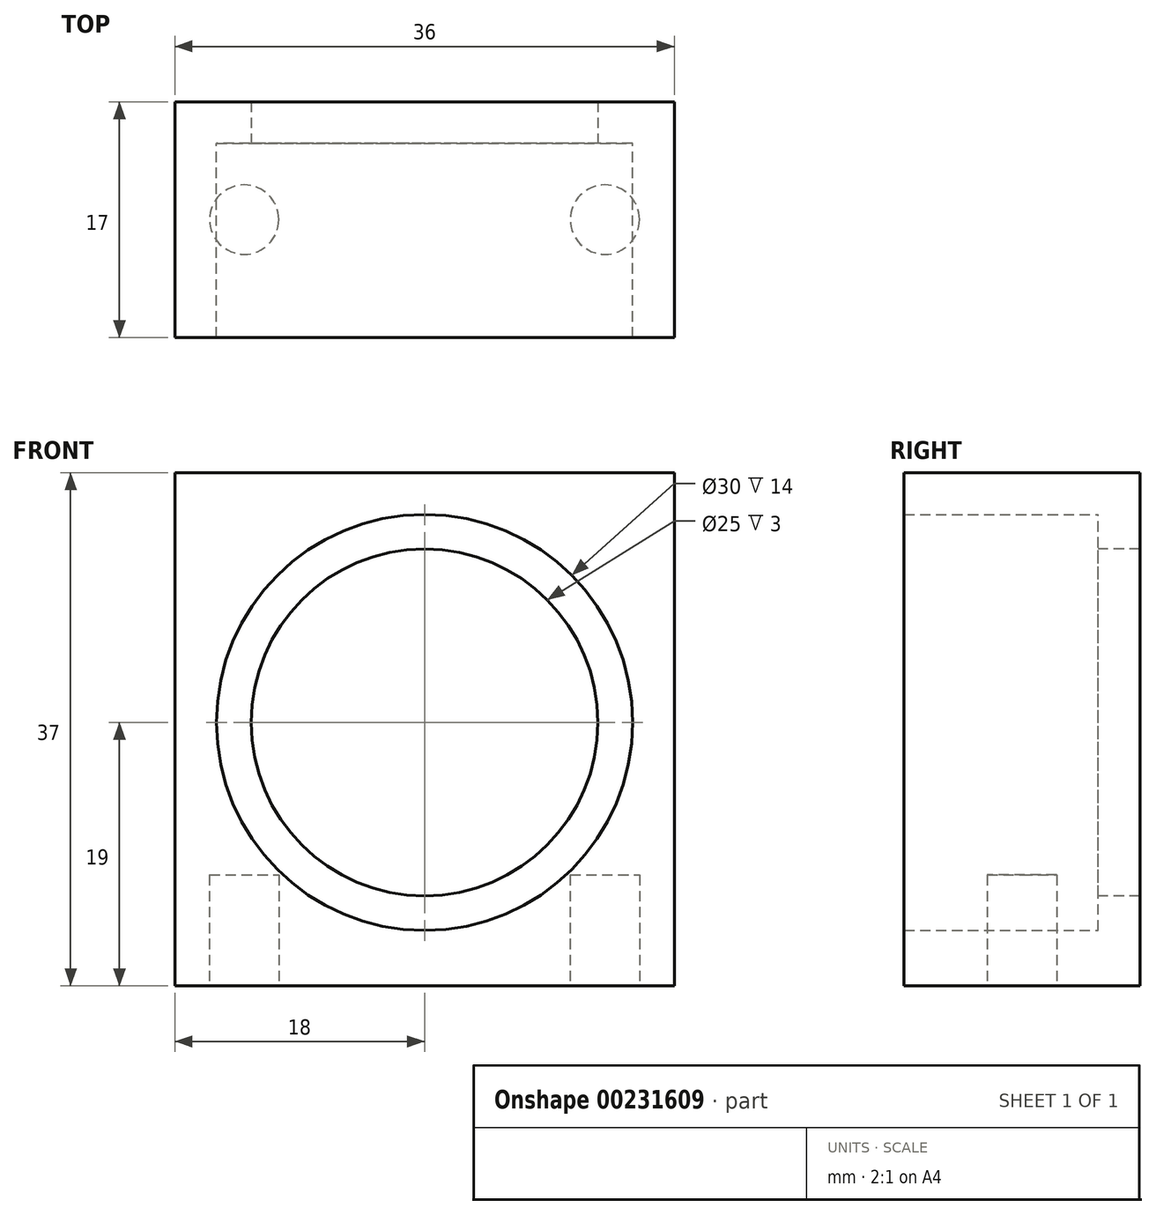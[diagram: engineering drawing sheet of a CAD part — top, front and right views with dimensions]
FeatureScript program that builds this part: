
annotation { "Feature Type Name" : "Feature", "Feature Type Description" : "" }
export const myFeature = defineFeature(function(context is Context, id is Id, definition is map)
    precondition{}
    {
        {
            var Q0;
            Q0=qCreatedBy(makeId("Front.planeOp"),FACE);
            var sketch = newSketch(context, id + "F0", { "sketchPlane" : qUnion([Q0])});
            skCircle(sketch, "E0", {"center": v(0, 0) * mm, "radius": 12.5 * mm});
            skCircle(sketch, "E1", {"center": v(0, 0) * mm, "radius": 15 * mm});
            skLineSegment(sketch, "E2.bottom", {"start": v(-18, 18) * mm, "end": v(18, 18) * mm});
            skLineSegment(sketch, "E2.top", {"start": v(-18, -19) * mm, "end": v(18, -19) * mm});
            skLineSegment(sketch, "E2.left", {"start": v(-18, 18) * mm, "end": v(-18, -19) * mm});
            skLineSegment(sketch, "E2.right", {"start": v(18, 18) * mm, "end": v(18, -19) * mm});
            skSolve(sketch);
        }
        {
            var Q0;
            Q0=makeQuery(id+"F0.imprint","IMPRINT",FACE,{"disambiguationData":[TD([[makeQuery(id+"F0.imprint","IMPRINT",EDGE,{"derivedFrom":sQuery(id+"F0.wireOp",EDGE,"E1")}),-1.0]])]});
            extrude(context, id + "F1", {"entities" : qUnion([Q0]), "depth" : 14 * mm});
        }
        {
            var Q0;
            Q0=makeQuery(id+"F0.imprint","IMPRINT",FACE,{"disambiguationData":[TD([[makeQuery(id+"F0.imprint","IMPRINT",EDGE,{"derivedFrom":sQuery(id+"F0.wireOp",EDGE,"E0")}),-1.0]])]});
            var Q1;
            Q1=makeQuery(id+"F0.imprint","IMPRINT",FACE,{"disambiguationData":[TD([[makeQuery(id+"F0.imprint","IMPRINT",EDGE,{"derivedFrom":sQuery(id+"F0.wireOp",EDGE,"E1")}),-1.0]])]});
            extrude(context, id + "F2", {"entities" : qUnion([Q0, Q1]), "operationType" : NewBodyOperationType.ADD, "oppositeDirection" : true, "depth" : 3 * mm});
        }
        {
            var Q0;
            {var subQ0=sQuery(id+"F0.wireOp",EDGE,"E2.top");Q0=makeQuery(id+"F2.boolean.opBoolean","MERGE",FACE,{"derivedFrom":[makeQuery(id+"F1.opExtrude","SWEPT_FACE",FACE,{"disambiguationData":[OSD([subQ0])]}),makeQuery(id+"F2.opExtrude","SWEPT_FACE",FACE,{"disambiguationData":[OSD([subQ0])]})]});}
            var sketch = newSketch(context, id + "F3", { "sketchPlane" : qUnion([Q0])});
            skLineSegment(sketch, "E3", {"start": v(-18, 5.5) * mm, "end": v(18, 5.5) * mm, "construction": true});
            skCircle(sketch, "E4", {"center": v(-13, 5.5) * mm, "radius": 2.5 * mm});
            skCircle(sketch, "E5", {"center": v(13, 5.5) * mm, "radius": 2.5 * mm});
            skSolve(sketch);
        }
        {
            var Q0;
            Q0 = qSketchRegion(id + "F3", true);
            extrude(context, id + "F4", {"entities" : qUnion([Q0]), "operationType" : NewBodyOperationType.REMOVE, "oppositeDirection" : true, "depth" : 8 * mm});
        }
    });
